# Revit family: Electrical-Box_FSR_OWB-CP1_FlushMount
name_source: partatom
category: Electrical Fixtures
units: mm (PartAtom-declared; Revit-internal decimal feet)

## family parameters
Always vertical = Yes
Classification Number = 23.85.10.17.11
Cut with Voids When Loaded = No
Host = Wall
Maintain Annotation Orientation = No
Part Type = Normal
Room Calculation Point = No
Round Connector Dimension = Use Diameter
Shared = No

## types (10) — shared parameters
Assembly Code = D5020100
Body Material = Material and Finish as Specified in 26 27 26
Building Codes = ftp://doclib.fsrinc.com/
Construction Details = ftp://doclib.fsrinc.com/
Cover Material = Material and Finish as Specified in 26 27 26
Default Elevation = 0"
Description = Electrical Box as Specified in 26 27 26
Embedment = 4"
Glazing = Translucent Plastic
Green Building-LEED = http://www.arcat.com
Gross Depth = 5"
Gross Height = 9 1/2"
Gross Projection = 1 1/2"
Gross Width = 9 1/2"
Installation-Fabrication = ftp://doclib.fsrinc.com/
Keynote = 26 27 26
Manufacturer = FSR Inc.
Manufacturer Fax = 973-785-4207
Manufacturer Website = http://www.fsrinc.com
Model = As Specified in 26 27 26
Product Data = http://www.arcat.com
Sales Information = http://www.fsrinc.com
Specification = http://www.arcat.com
Test Data = ftp://doclib.fsrinc.com/
Trim Material = Material and Finish as Specified in 26 27 26
URL = http://www.fsrinc.com
zero-valued in all types: Expected Lifespan (Years), Maintenance Schedule (Months), Warranty Duration (Years)

## per-type parameters (varying)
| type | Box Type | Internal Plate Type |
| OWB-CP1-W-BPLT | OWB-CP1-W_Box | Internal Plate : Blank Panel |
| OWB-CP1-W-NXD5 | OWB-CP1-W_Box | Internal Plate : AMX NXD 5" Touch Panel |
| OWB-CP1-W-TPS2000 | OWB-CP1-W_Box | Internal Plate : Crestron TPS2000 |
| OWB-CP1-W-TPS4L | OWB-CP1-W_Box | Internal Plate : Crestron TPS4L |
| OWB-CP1-W | OWB-CP1-W_Box | Internal Plate : None |
| OWB-CP1-BPLT | OWB-CP1_Box | Internal Plate : Blank Panel |
| OWB-CP1-NXD5 | OWB-CP1_Box | Internal Plate : AMX NXD 5" Touch Panel |
| OWB-CP1-TPS2000 | OWB-CP1_Box | Internal Plate : Crestron TPS2000 |
| OWB-CP1-TPS4L | OWB-CP1_Box | Internal Plate : Crestron TPS4L |
| OWB-CP1 | OWB-CP1_Box | Internal Plate : None |

## geometry (parser evidence)
native form markers: Sweep x14
no freeform markers — native parametric forms only
